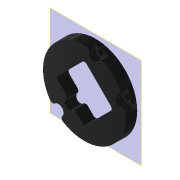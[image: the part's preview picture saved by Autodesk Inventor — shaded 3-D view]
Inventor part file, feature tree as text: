
AUTODESK INVENTOR PART (.ipt)
format: ipt  version: 2022 (Build 260153000, 153)  size: 310,272 bytes
history: native  units: in
note: dims shown in document units (in); Inventor stores cm internally (conversion verified against a paired STEP export)
features: reference x9, other x7, sketch x3, extrude x2, plane x1, hole x1, fillet x1, projected_geometry x1
ambient origin geometry x8: Origin, YZ Plane, XZ Plane, XY Plane, X Axis, Y Axis, Z Axis, Center Point
bodies: Solid1 (feature_tree)
feature tree (25):
  plane  "Work Plane1"
  extrude  "Extrusion1"  Depth=0.9843in
  hole  "Bohrung1"  [1 undecoded]
  fillet  "Rundung1"  Radius=0.9843in
  extrude  "Extrusion4"  Depth=0.0069in
  sketch  "Sketch1"  dims[d0=0.2756in d1=-0.0069in]
  reference  "Reference1"
  reference  "Reference5"
  reference  "Reference6"
  reference  "Reference7"
  sketch  "Skizze4"  dims[d9=0.1417in d10=0.75in d11=0.2559in d12=0.1575in d13=0.5635in d14=1.0in d15=0.8108in d17=0.9843in]
  reference  "Referenz9"
  reference  "Referenz10"
  reference  "Referenz11"
  reference  "Referenz12"
  reference  "Referenz13"
  sketch  "Skizze6"  dims[d18=0.9843in d19=45.0deg d20=0.9843in d21=0.0787in d22=0.0787in d23=0.1102in d24=0.1102in d25=0.1575in d26=0.1575in d27=0.1575in d28=0.0014in d29=0.0069in]
  projected_geometry  "Projizierte Kontur1"
  other  "<userpath>\Documents\Matchboxscope\INVENTOR\Matchboxscope_v1.iam"
  other  "Matchboxscope_v1.iam"
  other  "Matchboxscope_middle2_v1:1"
  other  "Matchboxscope_VCM_v1.iam"
  other  "Matchboxscope_middle2_m12VCMLens_v2:1"
  other  "Assembly_Matchboxscope_injectionmolded.iam"
  other  "IM_Matchboxscope_base:1"
note: 1 required parameter value undecoded (feature->parameter linkage not recoverable at this tier; creation-order binding heuristic only, values carry confidence <= 0.55)
